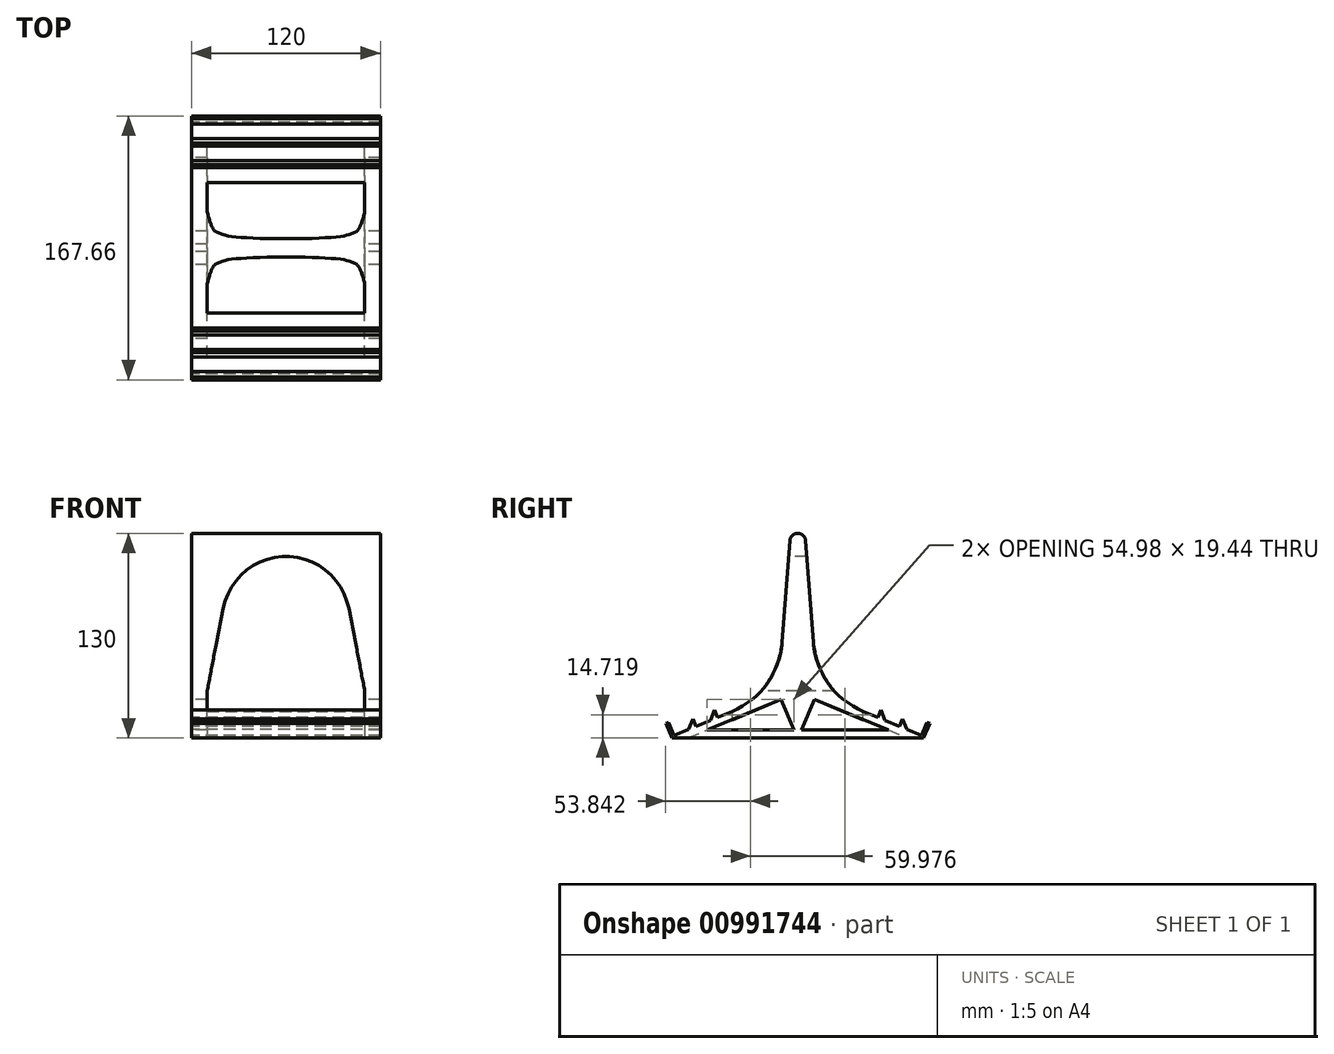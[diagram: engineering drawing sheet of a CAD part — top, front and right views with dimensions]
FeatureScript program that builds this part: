
annotation { "Feature Type Name" : "Feature", "Feature Type Description" : "" }
export const myFeature = defineFeature(function(context is Context, id is Id, definition is map)
    precondition{}
    {
        {
            var Q0;
            Q0=qCreatedBy(makeId("Right.planeOp"),FACE);
            var sketch = newSketch(context, id + "F0", { "sketchPlane" : qUnion([Q0])});
            skLineSegment(sketch, "E0", {"start": v(0, 0) * mm, "end": v(80, 0) * mm});
            skLineSegment(sketch, "E1", {"start": v(80, 0) * mm, "end": v(83.83, 9.24) * mm});
            skLineSegment(sketch, "E2", {"start": v(83.83, 9.24) * mm, "end": v(81.98, 10) * mm});
            skLineSegment(sketch, "E3", {"start": v(81.98, 10) * mm, "end": v(78.53, 1.69) * mm});
            skLineSegment(sketch, "E4", {"start": v(78.53, 1.69) * mm, "end": v(69.3, 5.52) * mm});
            skLineSegment(sketch, "E5", {"start": v(64.68, 7.43) * mm, "end": v(66.6, 12.05) * mm});
            skLineSegment(sketch, "E6", {"start": v(66.6, 12.05) * mm, "end": v(69.3, 5.52) * mm});
            skArc(sketch, "E7", {"start": v(4.99, 125.39) * mm, "mid": v(3.4, 128.67) * mm, "end": v(0, 130) * mm});
            skLineSegment(sketch, "E8", {"start": v(0, 0) * mm, "end": v(0, 130) * mm, "construction": true});
            skLineSegment(sketch, "E9", {"start": v(50.82, 13.17) * mm, "end": v(52.73, 17.79) * mm});
            skLineSegment(sketch, "E10", {"start": v(52.73, 17.79) * mm, "end": v(55.44, 11.26) * mm});
            skLineSegment(sketch, "E11", {"start": v(4.99, 125.39) * mm, "end": v(10, 60.53) * mm});
            skArc(sketch, "E12", {"start": v(10, 60.53) * mm, "mid": v(19.64, 34.3) * mm, "end": v(41.58, 17) * mm});
            skLineSegment(sketch, "E13.trimOffspring", {"start": v(50.82, 13.17) * mm, "end": v(41.58, 17) * mm});
            skLineSegment(sketch, "E14.trimOffspring", {"start": v(64.68, 7.43) * mm, "end": v(55.44, 11.26) * mm});
            skLineSegment(sketch, "E15", {"start": v(0, 5) * mm, "end": v(57.48, 5) * mm});
            skLineSegment(sketch, "E16", {"start": v(57.48, 5) * mm, "end": v(10.55, 24.44) * mm});
            skLineSegment(sketch, "E17.MirrorCS", {"start": v(-50.82, 13.17) * mm, "end": v(-52.73, 17.79) * mm});
            skLineSegment(sketch, "E18.MirrorCS", {"start": v(-83.83, 9.24) * mm, "end": v(-81.98, 10) * mm});
            skLineSegment(sketch, "E19.MirrorCS", {"start": v(-64.68, 7.43) * mm, "end": v(-66.6, 12.05) * mm});
            skLineSegment(sketch, "E20.MirrorCS", {"start": v(-66.6, 12.05) * mm, "end": v(-69.3, 5.52) * mm});
            skArc(sketch, "E21.MirrorCS", {"start": v(-10, 60.53) * mm, "mid": v(-19.64, 34.3) * mm, "end": v(-41.58, 17) * mm});
            skLineSegment(sketch, "E22.MirrorCS", {"start": v(-64.68, 7.43) * mm, "end": v(-55.44, 11.26) * mm});
            skLineSegment(sketch, "E23.MirrorCS", {"start": v(-50.82, 13.17) * mm, "end": v(-41.58, 17) * mm});
            skArc(sketch, "E24.MirrorCS", {"start": v(-4.99, 125.39) * mm, "mid": v(-3.4, 128.67) * mm, "end": v(0, 130) * mm});
            skLineSegment(sketch, "E25.MirrorCS", {"start": v(-52.73, 17.79) * mm, "end": v(-55.44, 11.26) * mm});
            skLineSegment(sketch, "E26.MirrorCS", {"start": v(-4.99, 125.39) * mm, "end": v(-10, 60.53) * mm});
            skLineSegment(sketch, "E27.MirrorCS", {"start": v(0, 5) * mm, "end": v(-57.48, 5) * mm});
            skLineSegment(sketch, "E28.MirrorCS", {"start": v(-78.53, 1.69) * mm, "end": v(-69.3, 5.52) * mm});
            skLineSegment(sketch, "E29.MirrorCS", {"start": v(-80, 0) * mm, "end": v(-83.83, 9.24) * mm});
            skLineSegment(sketch, "E30.MirrorCS", {"start": v(-81.98, 10) * mm, "end": v(-78.53, 1.69) * mm});
            skLineSegment(sketch, "E31.MirrorCS", {"start": v(0, 0) * mm, "end": v(-80, 0) * mm});
            skLineSegment(sketch, "E32.MirrorCS", {"start": v(-57.48, 5) * mm, "end": v(-10.55, 24.44) * mm});
            skLineSegment(sketch, "E33", {"start": v(-10.55, 24.44) * mm, "end": v(-2.5, 5) * mm});
            skLineSegment(sketch, "E34", {"start": v(2.5, 5) * mm, "end": v(10.55, 24.44) * mm});
            skSolve(sketch);
        }
        {
            var Q0;
            Q0=makeQuery(id+"F0.imprint","IMPRINT",FACE,{"disambiguationData":[TD([[makeQuery(id+"F0.imprint","IMPRINT",EDGE,{"derivedFrom":sQuery(id+"F0.wireOp",EDGE,"E0")}),1.0]])]});
            extrude(context, id + "F1", {"entities" : qUnion([Q0]), "endBound" : BoundingType.SYMMETRIC, "depth" : 120 * mm, "offsetDistance" : 25 * mm});
        }
        {
            var Q0;
            Q0=qCreatedBy(makeId("Front.planeOp"),FACE);
            var sketch = newSketch(context, id + "F2", { "sketchPlane" : qUnion([Q0])});
            skLineSegment(sketch, "E35", {"start": v(0, 0) * mm, "end": v(0, 194.16) * mm, "construction": true});
            skArc(sketch, "E36", {"start": v(-40, 82.3) * mm, "mid": v(-25.95, 106.04) * mm, "end": v(0, 115.39) * mm});
            skLineSegment(sketch, "E37", {"start": v(-40, 82.3) * mm, "end": v(-50, 30) * mm});
            skLineSegment(sketch, "E38", {"start": v(-50, 30) * mm, "end": v(0, 30) * mm});
            skLineSegment(sketch, "E39.MirrorCS", {"start": v(40, 82.3) * mm, "end": v(50, 30) * mm});
            skLineSegment(sketch, "E40.MirrorCS", {"start": v(50, 30) * mm, "end": v(0, 30) * mm});
            skArc(sketch, "E41.MirrorCS", {"start": v(40, 82.3) * mm, "mid": v(25.95, 106.04) * mm, "end": v(0, 115.39) * mm});
            skSolve(sketch);
        }
        {
            var Q0;
            Q0 = qSketchRegion(id + "F2", true);
            extrude(context, id + "F3", {"entities" : qUnion([Q0]), "operationType" : NewBodyOperationType.REMOVE, "endBound" : BoundingType.SYMMETRIC, "oppositeDirection" : true, "depth" : 50 * mm, "offsetDistance" : 25 * mm});
        }
        {
            var Q0;
            Q0=makeQuery(id+"F3.boolean.opBoolean","COPY",FACE,{"derivedFrom":makeQuery(id+"F3.opExtrude","SWEPT_FACE",FACE,{"disambiguationData":[OSD([sQuery(id+"F2.wireOp",EDGE,"E38"),sQuery(id+"F2.wireOp",EDGE,"E40.MirrorCS")])]})});
            var sketch = newSketch(context, id + "F4", { "sketchPlane" : qUnion([Q0])});
            skLineSegment(sketch, "E42.bottom", {"start": v(-50, 41.58) * mm, "end": v(50, 41.58) * mm});
            skLineSegment(sketch, "E42.top", {"start": v(-50, 0) * mm, "end": v(50, 0) * mm});
            skLineSegment(sketch, "E42.left", {"start": v(-50, 41.58) * mm, "end": v(-50, 0) * mm});
            skLineSegment(sketch, "E42.right", {"start": v(50, 41.58) * mm, "end": v(50, 0) * mm});
            skLineSegment(sketch, "E43.MirrorCS", {"start": v(-50, -41.58) * mm, "end": v(-50, 0) * mm});
            skLineSegment(sketch, "E44.MirrorCS", {"start": v(-50, -41.58) * mm, "end": v(50, -41.58) * mm});
            skLineSegment(sketch, "E45.MirrorCS", {"start": v(50, -41.58) * mm, "end": v(50, 0) * mm});
            skSolve(sketch);
        }
        {
            var Q0;
            Q0 = qSketchRegion(id + "F4", true);
            extrude(context, id + "F5", {"entities" : qUnion([Q0]), "operationType" : NewBodyOperationType.REMOVE, "endBound" : BoundingType.THROUGH_ALL, "oppositeDirection" : true, "depth" : 25 * mm, "offsetDistance" : 25 * mm});
        }
        {
            var Q0;
            Q0=makeQuery(id+"F5.boolean.opBoolean","COPY",FACE,{"disambiguationData":[TD([makeQuery(id+"F1.opExtrude","SWEPT_FACE",FACE,{"disambiguationData":[OSD([sQuery(id+"F0.wireOp",EDGE,"E15")])]})])],"derivedFrom":makeQuery(id+"F5.opExtrude","SWEPT_FACE",FACE,{"disambiguationData":[OSD([sQuery(id+"F4.wireOp",EDGE,"E42.bottom")])]})});
            var Q1;
            Q1=makeQuery(id+"F1.opExtrude","SWEPT_FACE",FACE,{"disambiguationData":[OSD([sQuery(id+"F0.wireOp",EDGE,"E16")])]});
            extrude(context, id + "F6", {"entities" : qUnion([Q0]), "operationType" : NewBodyOperationType.REMOVE, "endBound" : BoundingType.UP_TO_SURFACE, "oppositeDirection" : true, "depth" : 17.9 * mm, "endBoundEntityFace" : qUnion([Q1]), "offsetDistance" : 25 * mm});
        }
        {
            var Q0;
            Q0=makeQuery(id+"F5.boolean.opBoolean","COPY",FACE,{"disambiguationData":[TD([makeQuery(id+"F1.opExtrude","SWEPT_FACE",FACE,{"disambiguationData":[OSD([sQuery(id+"F0.wireOp",EDGE,"E27.MirrorCS")])]})])],"derivedFrom":makeQuery(id+"F5.opExtrude","SWEPT_FACE",FACE,{"disambiguationData":[OSD([sQuery(id+"F4.wireOp",EDGE,"E44.MirrorCS")])]})});
            var Q1;
            Q1=makeQuery(id+"F1.opExtrude","SWEPT_FACE",FACE,{"disambiguationData":[OSD([sQuery(id+"F0.wireOp",EDGE,"E32.MirrorCS")])]});
            extrude(context, id + "F7", {"entities" : qUnion([Q0]), "operationType" : NewBodyOperationType.REMOVE, "endBound" : BoundingType.UP_TO_SURFACE, "oppositeDirection" : true, "depth" : 25 * mm, "endBoundEntityFace" : qUnion([Q1]), "offsetDistance" : 25 * mm});
        }
    });
